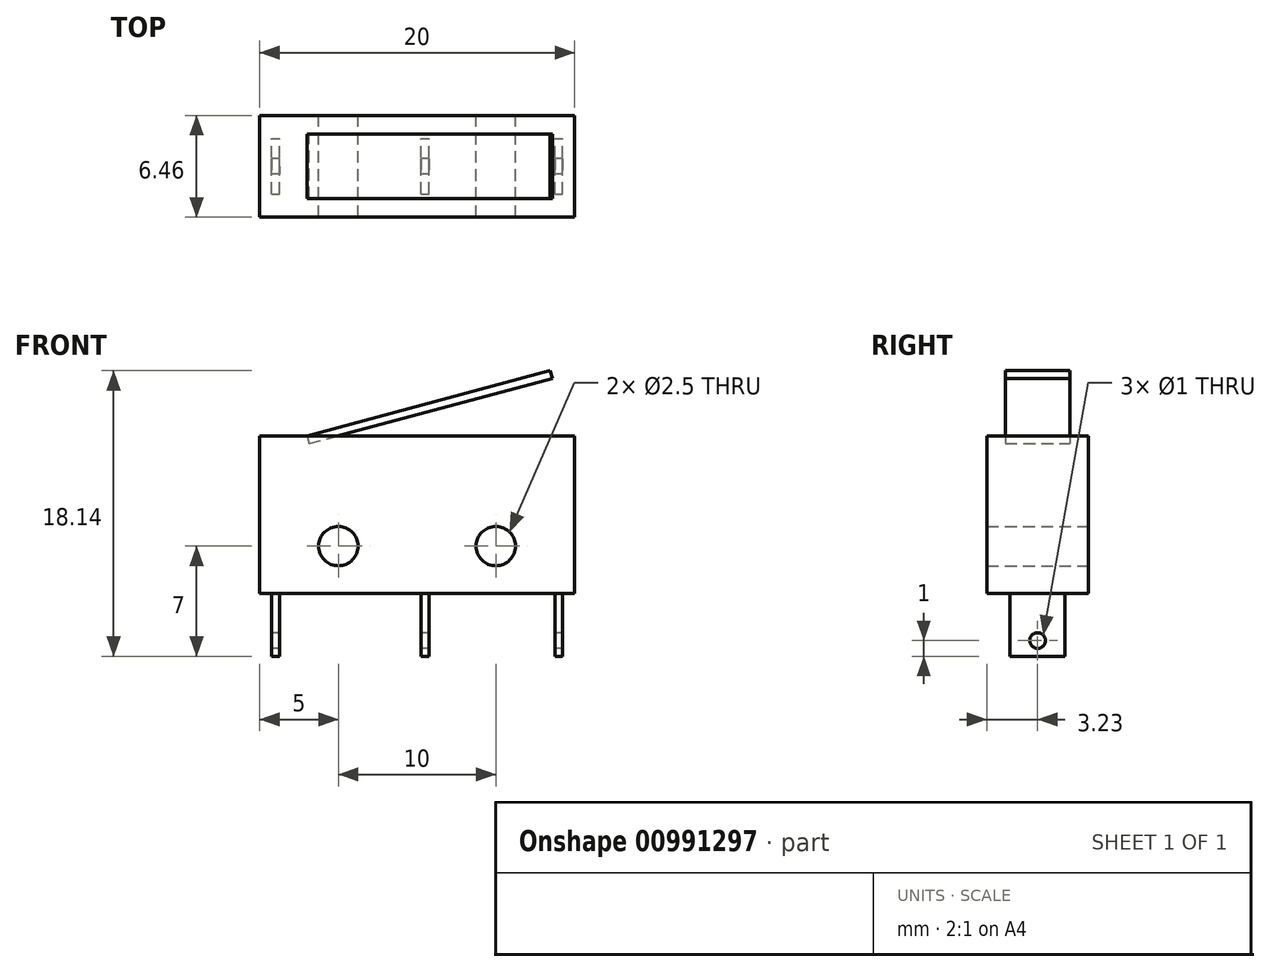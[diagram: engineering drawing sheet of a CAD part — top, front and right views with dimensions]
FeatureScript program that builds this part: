
annotation { "Feature Type Name" : "Feature", "Feature Type Description" : "" }
export const myFeature = defineFeature(function(context is Context, id is Id, definition is map)
    precondition{}
    {
        {
            var Q0;
            Q0=qCreatedBy(makeId("Front.planeOp"),FACE);
            var sketch = newSketch(context, id + "F0", { "sketchPlane" : qUnion([Q0])});
            skLineSegment(sketch, "E0.bottom", {"start": v(-10, 0) * mm, "end": v(10, 0) * mm});
            skLineSegment(sketch, "E0.top", {"start": v(-10, 10) * mm, "end": v(10, 10) * mm});
            skLineSegment(sketch, "E0.left", {"start": v(-10, 0) * mm, "end": v(-10, 10) * mm});
            skLineSegment(sketch, "E0.right", {"start": v(10, 0) * mm, "end": v(10, 10) * mm});
            skPoint(sketch, "E0.middle", {"position": v(0, 5) * mm});
            skCircle(sketch, "E1", {"center": v(-5, 3) * mm, "radius": 1.25 * mm});
            skCircle(sketch, "E2.MirrorC", {"center": v(5, 3) * mm, "radius": 1.25 * mm});
            skSolve(sketch);
        }
        {
            var Q0;
            Q0=makeQuery(id+"F0.imprint","IMPRINT",FACE,{"disambiguationData":[TD([[makeQuery(id+"F0.imprint","IMPRINT",EDGE,{"derivedFrom":sQuery(id+"F0.wireOp",EDGE,"E0.bottom")}),1.0]])]});
            extrude(context, id + "F1", {"entities" : qUnion([Q0]), "depth" : 6.45 * mm, "offsetDistance" : 25 * mm, "symmetric" : true});
        }
        {
            var Q0;
            Q0=qCreatedBy(makeId("Front.planeOp"),FACE);
            var sketch = newSketch(context, id + "F2", { "sketchPlane" : qUnion([Q0])});
            skLineSegment(sketch, "E3", {"start": v(-7, 10) * mm, "end": v(-6.87, 9.52) * mm});
            skLineSegment(sketch, "E4", {"start": v(-6.87, 9.52) * mm, "end": v(8.58, 13.66) * mm});
            skLineSegment(sketch, "E5", {"start": v(8.58, 13.66) * mm, "end": v(8.45, 14.14) * mm});
            skLineSegment(sketch, "E6", {"start": v(8.45, 14.14) * mm, "end": v(-7, 10) * mm});
            skSolve(sketch);
        }
        {
            var Q0;
            Q0=makeQuery(id+"F2.imprint","IMPRINT",FACE,{"disambiguationData":[TD([[makeQuery(id+"F2.imprint","IMPRINT",EDGE,{"derivedFrom":sQuery(id+"F2.wireOp",EDGE,"E3")}),1.0]])]});
            extrude(context, id + "F3", {"entities" : qUnion([Q0]), "depth" : 4.1 * mm, "offsetDistance" : 25 * mm, "symmetric" : true});
        }
        {
            var Q0;
            Q0=qCreatedBy(makeId("Front.planeOp"),FACE);
            var sketch = newSketch(context, id + "F4", { "sketchPlane" : qUnion([Q0])});
            skLineSegment(sketch, "E7.bottom", {"start": v(-9.25, 0) * mm, "end": v(-8.75, 0) * mm});
            skLineSegment(sketch, "E7.top", {"start": v(-9.25, -4) * mm, "end": v(-8.75, -4) * mm});
            skLineSegment(sketch, "E7.left", {"start": v(-9.25, 0) * mm, "end": v(-9.25, -4) * mm});
            skLineSegment(sketch, "E7.right", {"start": v(-8.75, 0) * mm, "end": v(-8.75, -4) * mm});
            skLineSegment(sketch, "E8.bottom", {"start": v(8.75, 0) * mm, "end": v(9.25, 0) * mm});
            skLineSegment(sketch, "E8.top", {"start": v(8.75, -4) * mm, "end": v(9.25, -4) * mm});
            skLineSegment(sketch, "E8.left", {"start": v(8.75, 0) * mm, "end": v(8.75, -4) * mm});
            skLineSegment(sketch, "E8.right", {"start": v(9.25, 0) * mm, "end": v(9.25, -4) * mm});
            skLineSegment(sketch, "E9.bottom", {"start": v(0.25, 0) * mm, "end": v(0.75, 0) * mm});
            skLineSegment(sketch, "E9.top", {"start": v(0.25, -4) * mm, "end": v(0.75, -4) * mm});
            skLineSegment(sketch, "E9.left", {"start": v(0.25, 0) * mm, "end": v(0.25, -4) * mm});
            skLineSegment(sketch, "E9.right", {"start": v(0.75, 0) * mm, "end": v(0.75, -4) * mm});
            skSolve(sketch);
        }
        {
            var Q0;
            Q0=makeQuery(id+"F4.imprint","IMPRINT",FACE,{"disambiguationData":[TD([[makeQuery(id+"F4.imprint","IMPRINT",EDGE,{"derivedFrom":sQuery(id+"F4.wireOp",EDGE,"E7.bottom")}),-1.0]])]});
            var Q1;
            Q1=makeQuery(id+"F4.imprint","IMPRINT",FACE,{"disambiguationData":[TD([[makeQuery(id+"F4.imprint","IMPRINT",EDGE,{"derivedFrom":sQuery(id+"F4.wireOp",EDGE,"E9.bottom")}),-1.0]])]});
            var Q2;
            Q2=makeQuery(id+"F4.imprint","IMPRINT",FACE,{"disambiguationData":[TD([[makeQuery(id+"F4.imprint","IMPRINT",EDGE,{"derivedFrom":sQuery(id+"F4.wireOp",EDGE,"E8.bottom")}),-1.0]])]});
            extrude(context, id + "F5", {"entities" : qUnion([Q0, Q1, Q2]), "depth" : 3.5 * mm, "offsetDistance" : 25 * mm, "symmetric" : true});
        }
        {
            var Q0;
            Q0=makeQuery(id+"F5.opExtrude","SWEPT_FACE",FACE,{"disambiguationData":[OSD([sQuery(id+"F4.wireOp",EDGE,"E7.left")])]});
            var sketch = newSketch(context, id + "F6", { "sketchPlane" : qUnion([Q0])});
            skCircle(sketch, "E10", {"center": v(0, -3) * mm, "radius": 0.5 * mm});
            skSolve(sketch);
        }
        {
            var Q0;
            Q0=makeQuery(id+"F6.imprint","IMPRINT",FACE,{"disambiguationData":[TD([[makeQuery(id+"F6.imprint","IMPRINT",EDGE,{"derivedFrom":sQuery(id+"F6.wireOp",EDGE,"E10")}),1.0]])]});
            extrude(context, id + "F7", {"entities" : qUnion([Q0]), "operationType" : NewBodyOperationType.REMOVE, "endBound" : BoundingType.THROUGH_ALL, "oppositeDirection" : true, "depth" : 25 * mm, "offsetDistance" : 25 * mm});
        }
    });
